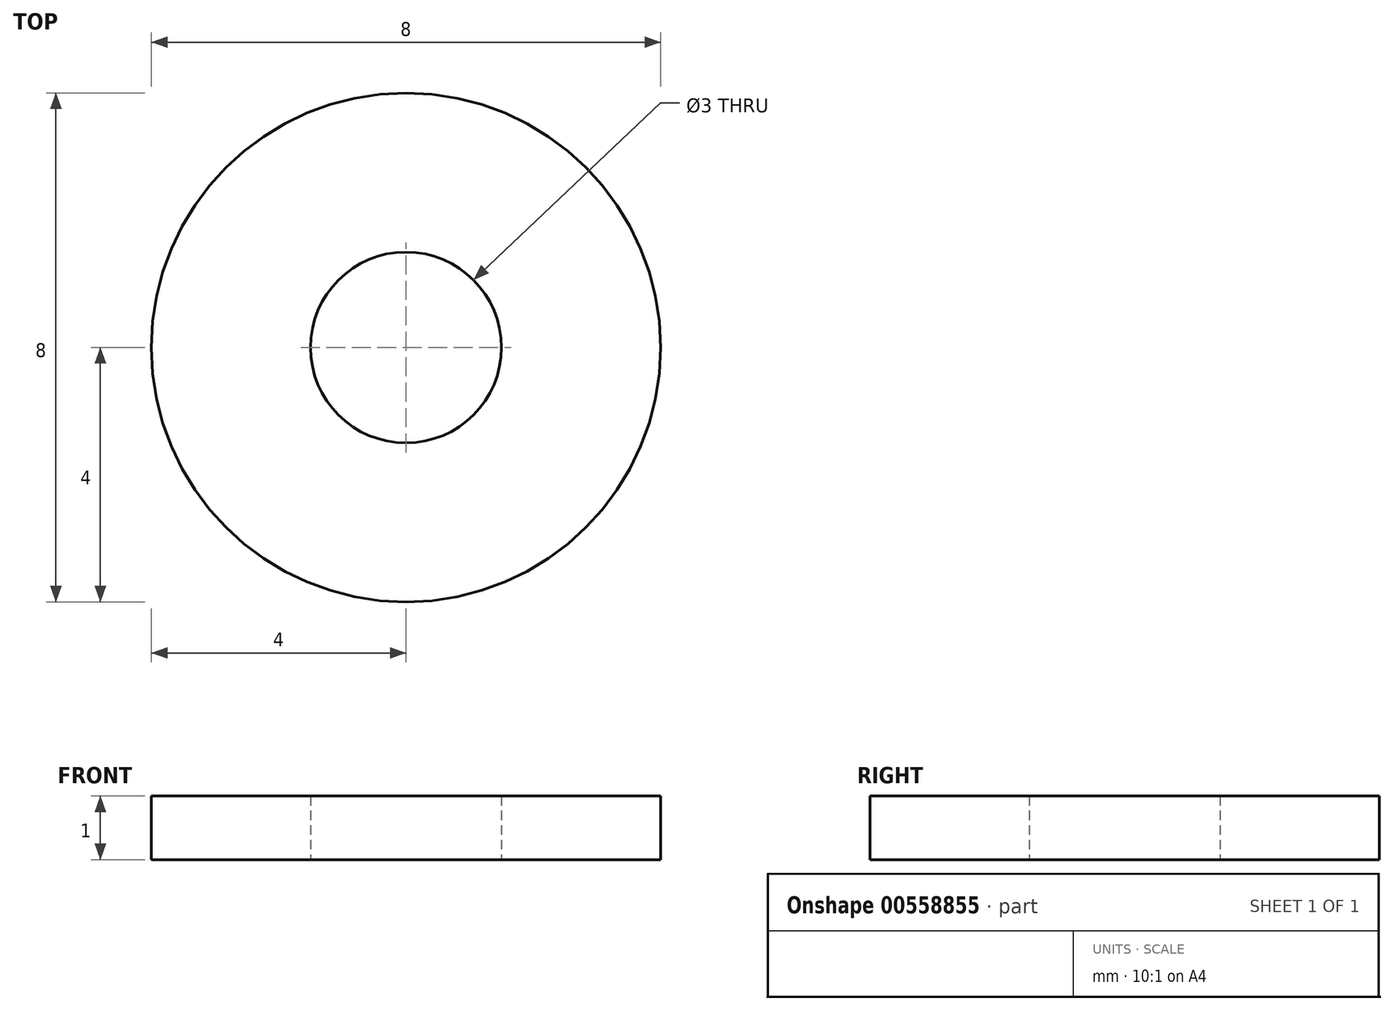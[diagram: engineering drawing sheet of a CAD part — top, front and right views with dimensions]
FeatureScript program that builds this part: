
annotation { "Feature Type Name" : "Feature", "Feature Type Description" : "" }
export const myFeature = defineFeature(function(context is Context, id is Id, definition is map)
    precondition{}
    {
        {
            var Q0;
            Q0=qCreatedBy(makeId("Top.planeOp"),FACE);
            var sketch = newSketch(context, id + "F0", { "sketchPlane" : qUnion([Q0])});
            skCircle(sketch, "E0", {"center": v(0, 0) * mm, "radius": 1.5 * mm});
            skCircle(sketch, "E1", {"center": v(0, 0) * mm, "radius": 4 * mm});
            skSolve(sketch);
        }
        {
            var Q0;
            Q0 = qSketchRegion(id + "F0", true);
            extrude(context, id + "F1", {"entities" : qUnion([Q0]), "depth" : 1 * mm, "offsetDistance" : 25 * mm});
        }
    });
